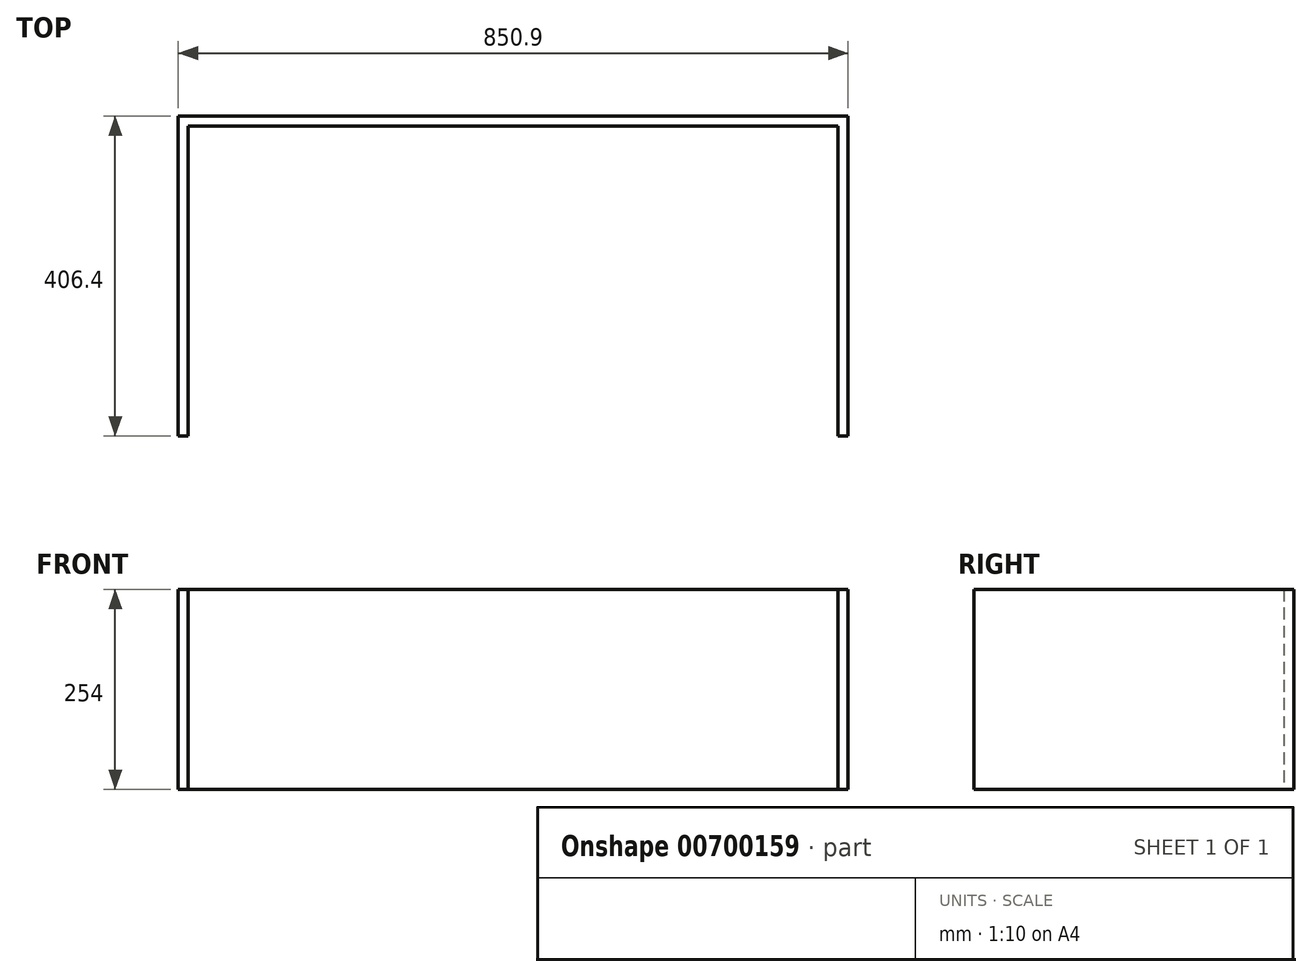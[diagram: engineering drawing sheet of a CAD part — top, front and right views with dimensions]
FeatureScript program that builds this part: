
annotation { "Feature Type Name" : "Feature", "Feature Type Description" : "" }
export const myFeature = defineFeature(function(context is Context, id is Id, definition is map)
    precondition{}
    {
        {
            var Q0;
            Q0=qCreatedBy(makeId("Top.planeOp"),FACE);
            var sketch = newSketch(context, id + "F0", { "sketchPlane" : qUnion([Q0])});
            skLineSegment(sketch, "E0.bottom", {"start": v(425.45, 203.2) * mm, "end": v(-425.45, 203.2) * mm});
            skLineSegment(sketch, "E0.top", {"start": v(425.45, -203.2) * mm, "end": v(-425.45, -203.2) * mm});
            skLineSegment(sketch, "E0.left", {"start": v(425.45, 203.2) * mm, "end": v(425.45, -203.2) * mm});
            skLineSegment(sketch, "E0.right", {"start": v(-425.45, 203.2) * mm, "end": v(-425.45, -203.2) * mm});
            skPoint(sketch, "E0.middle", {"position": v(0, 0) * mm});
            skLineSegment(sketch, "E1.bottom", {"start": v(-412.75, 190.5) * mm, "end": v(412.75, 190.5) * mm});
            skLineSegment(sketch, "E1.top", {"start": v(-412.75, -190.5) * mm, "end": v(412.75, -190.5) * mm});
            skLineSegment(sketch, "E1.left", {"start": v(-412.75, 190.5) * mm, "end": v(-412.75, -190.5) * mm});
            skLineSegment(sketch, "E1.right", {"start": v(412.75, 190.5) * mm, "end": v(412.75, -190.5) * mm});
            skLineSegment(sketch, "E2", {"start": v(-412.75, -190.5) * mm, "end": v(-412.75, -203.2) * mm});
            skLineSegment(sketch, "E3", {"start": v(412.75, -190.5) * mm, "end": v(412.75, -203.2) * mm});
            skSolve(sketch);
        }
        {
            var Q0;
            Q0=makeQuery(id+"F0.imprint","IMPRINT",FACE,{"disambiguationData":[TD([[makeQuery(id+"F0.imprint","IMPRINT",EDGE,{"derivedFrom":sQuery(id+"F0.wireOp",EDGE,"E0.bottom")}),1.0]])]});
            extrude(context, id + "F1", {"entities" : qUnion([Q0]), "depth" : 254 * mm, "offsetDistance" : 25.4 * mm});
        }
    });
